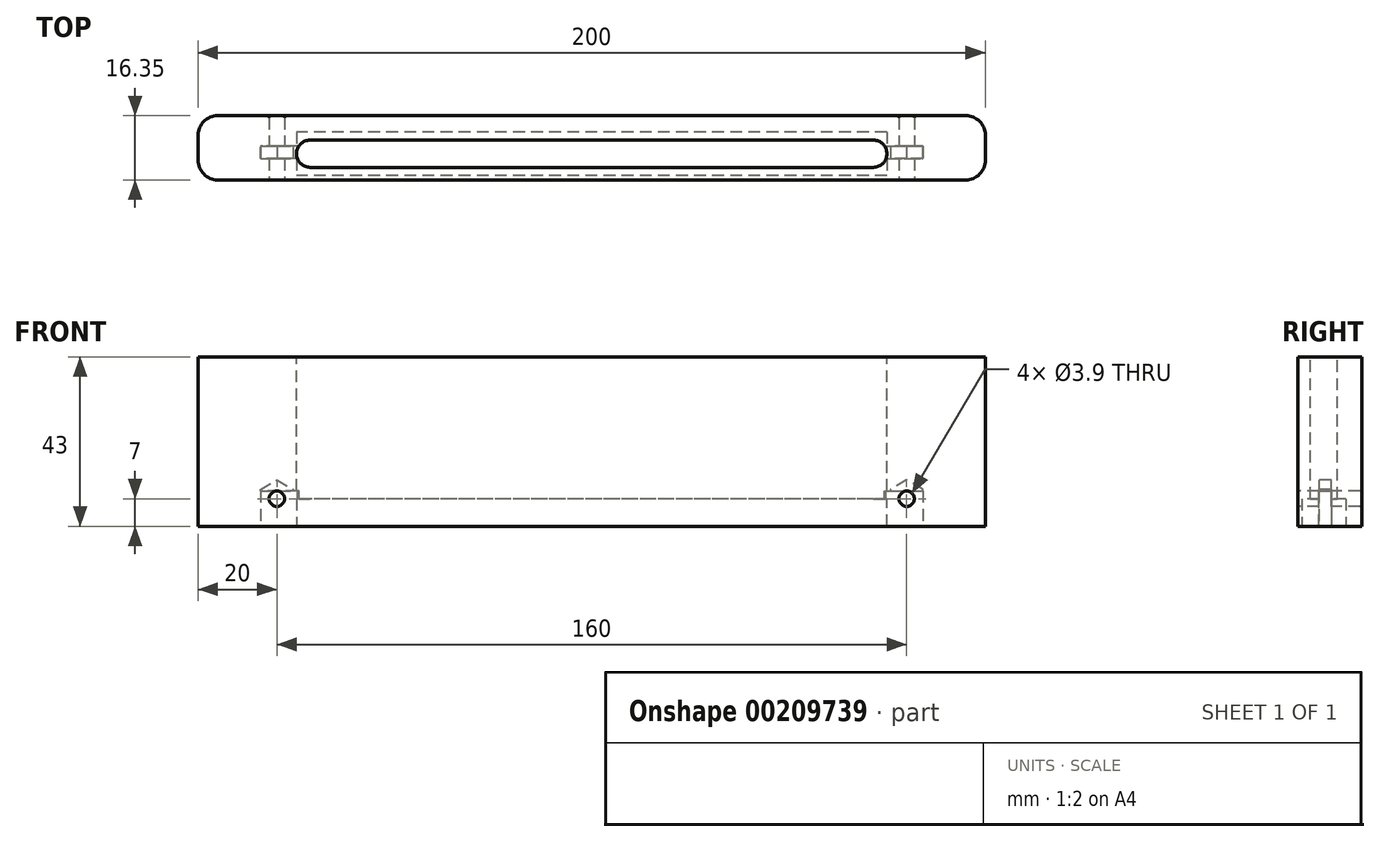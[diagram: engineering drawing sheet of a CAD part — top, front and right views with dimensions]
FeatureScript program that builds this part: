
annotation { "Feature Type Name" : "Feature", "Feature Type Description" : "" }
export const myFeature = defineFeature(function(context is Context, id is Id, definition is map)
    precondition{}
    {
        {
            var Q0;
            Q0=qCreatedBy(makeId("Top.planeOp"),FACE);
            var sketch = newSketch(context, id + "F0", { "sketchPlane" : qUnion([Q0])});
            skLineSegment(sketch, "E0.bottom", {"start": v(-100, 7) * mm, "end": v(100, 7) * mm});
            skLineSegment(sketch, "E0.top", {"start": v(-100, -7) * mm, "end": v(100, -7) * mm});
            skLineSegment(sketch, "E0.left", {"start": v(-100, 7) * mm, "end": v(-100, -7) * mm});
            skLineSegment(sketch, "E0.right", {"start": v(100, 7) * mm, "end": v(100, -7) * mm});
            skPoint(sketch, "E0.middle", {"position": v(0, 0) * mm});
            skLineSegment(sketch, "E1.top", {"start": v(-100, 9.35) * mm, "end": v(100, 9.35) * mm});
            skLineSegment(sketch, "E1.left", {"start": v(-100, 7) * mm, "end": v(-100, 9.35) * mm});
            skLineSegment(sketch, "E1.right", {"start": v(100, 7) * mm, "end": v(100, 9.35) * mm});
            skSolve(sketch);
        }
        {
            var Q0;
            Q0 = qSketchRegion(id + "F0", true);
            extrude(context, id + "F1", {"entities" : qUnion([Q0]), "depth" : 43 * mm});
        }
        {
            var Q0;
            Q0=makeQuery(id+"F1.opExtrude","CAP_FACE",FACE,{"disambiguationData":[OSD([sQuery(id+"F0.wireOp",EDGE,"E0.bottom"),sQuery(id+"F0.wireOp",EDGE,"E0.top"),sQuery(id+"F0.wireOp",EDGE,"E0.left"),sQuery(id+"F0.wireOp",EDGE,"E0.right")])],"isStart":false});
            var sketch = newSketch(context, id + "F2", { "sketchPlane" : qUnion([Q0])});
            skCircle(sketch, "E2", {"center": v(-22, 0) * mm, "radius": 3.45 * mm});
            skSolve(sketch);
        }
        {
            var Q0;
            Q0=makeQuery(id+"F1.opExtrude","CAP_FACE",FACE,{"disambiguationData":[OSD([sQuery(id+"F0.wireOp",EDGE,"E0.bottom"),sQuery(id+"F0.wireOp",EDGE,"E0.top"),sQuery(id+"F0.wireOp",EDGE,"E0.left"),sQuery(id+"F0.wireOp",EDGE,"E0.right")])],"isStart":true});
            var sketch = newSketch(context, id + "F3", { "sketchPlane" : qUnion([Q0])});
            skPoint(sketch, "E3", {"position": v(-22, 0) * mm});
            skPoint(sketch, "E4.MirrorP", {"position": v(22, 0) * mm});
            skLineSegment(sketch, "E5", {"start": v(-25.2, 5.54) * mm, "end": v(-18.8, 5.54) * mm});
            skLineSegment(sketch, "E6", {"start": v(-25.2, 5.54) * mm, "end": v(-28.4, 0) * mm});
            skLineSegment(sketch, "E7", {"start": v(-28.4, 0) * mm, "end": v(-25.2, -5.54) * mm});
            skLineSegment(sketch, "E8", {"start": v(-25.2, -5.54) * mm, "end": v(-18.8, -5.54) * mm});
            skLineSegment(sketch, "E9", {"start": v(-18.8, -5.54) * mm, "end": v(-15.6, 0) * mm});
            skLineSegment(sketch, "E10", {"start": v(-15.6, 0) * mm, "end": v(-18.8, 5.54) * mm});
            skLineSegment(sketch, "E11", {"start": v(-22, 0) * mm, "end": v(-22, 0) * mm, "construction": true});
            skPoint(sketch, "E11.startSnap0", {"position": v(-22, 5.54) * mm});
            skPoint(sketch, "E11.endSnap0", {"position": v(-22, -5.54) * mm});
            skLineSegment(sketch, "E12.MirrorCS", {"start": v(15.6, 0) * mm, "end": v(18.8, 5.54) * mm});
            skLineSegment(sketch, "E13.MirrorCS", {"start": v(25.2, 5.54) * mm, "end": v(18.8, 5.54) * mm});
            skLineSegment(sketch, "E14.MirrorCS", {"start": v(25.2, 5.54) * mm, "end": v(28.4, 0) * mm});
            skLineSegment(sketch, "E15.MirrorCS", {"start": v(28.4, 0) * mm, "end": v(25.2, -5.54) * mm});
            skLineSegment(sketch, "E16.MirrorCS", {"start": v(25.2, -5.54) * mm, "end": v(18.8, -5.54) * mm});
            skLineSegment(sketch, "E17.MirrorCS", {"start": v(18.8, -5.54) * mm, "end": v(15.6, 0) * mm});
            skSolve(sketch);
        }
        {
            var Q0;
            Q0=makeQuery(id+"F1.opExtrude","CAP_FACE",FACE,{"disambiguationData":[OSD([sQuery(id+"F0.wireOp",EDGE,"E0.bottom"),sQuery(id+"F0.wireOp",EDGE,"E0.top"),sQuery(id+"F0.wireOp",EDGE,"E0.left"),sQuery(id+"F0.wireOp",EDGE,"E0.right")])],"isStart":true});
            var sketch = newSketch(context, id + "F4", { "sketchPlane" : qUnion([Q0])});
            skLineSegment(sketch, "E18.bottom", {"start": v(75, -5.2) * mm, "end": v(-75, -5.2) * mm});
            skLineSegment(sketch, "E18.top", {"start": v(75, 5.9) * mm, "end": v(-75, 5.9) * mm});
            skLineSegment(sketch, "E18.left", {"start": v(75, -5.2) * mm, "end": v(75, 5.9) * mm});
            skLineSegment(sketch, "E18.right", {"start": v(-75, -5.2) * mm, "end": v(-75, 5.9) * mm});
            skPoint(sketch, "E18.middle", {"position": v(0, 0.35) * mm});
            skSolve(sketch);
        }
        {
            var Q0;
            Q0 = qSketchRegion(id + "F4", true);
            extrude(context, id + "F5", {"entities" : qUnion([Q0]), "operationType" : NewBodyOperationType.REMOVE, "oppositeDirection" : true, "depth" : 7 * mm});
        }
        {
            var Q0;
            Q0=makeQuery(id+"F1.opExtrude","SWEPT_FACE",FACE,{"disambiguationData":[OSD([sQuery(id+"F0.wireOp",EDGE,"E0.top")])]});
            var sketch = newSketch(context, id + "F6", { "sketchPlane" : qUnion([Q0])});
            skPoint(sketch, "E19", {"position": v(-80, 7) * mm});
            skPoint(sketch, "E20.MirrorP", {"position": v(80, 7) * mm});
            skCircle(sketch, "E21", {"center": v(-80, 7) * mm, "radius": 1.95 * mm});
            skCircle(sketch, "E22", {"center": v(80, 7) * mm, "radius": 1.95 * mm});
            skSolve(sketch);
        }
        {
            var Q0;
            Q0 = qSketchRegion(id + "F6", true);
            extrude(context, id + "F7", {"entities" : qUnion([Q0]), "operationType" : NewBodyOperationType.REMOVE, "endBound" : BoundingType.THROUGH_ALL, "oppositeDirection" : true, "depth" : 25 * mm});
        }
        {
            var Q0;
            Q0=makeQuery(id+"F1.opExtrude","CAP_FACE",FACE,{"disambiguationData":[OSD([sQuery(id+"F0.wireOp",EDGE,"E0.bottom"),sQuery(id+"F0.wireOp",EDGE,"E0.top"),sQuery(id+"F0.wireOp",EDGE,"E0.left"),sQuery(id+"F0.wireOp",EDGE,"E0.right")])],"isStart":false});
            var sketch = newSketch(context, id + "F8", { "sketchPlane" : qUnion([Q0])});
            skLineSegment(sketch, "E23", {"start": v(-71.55, -3.8) * mm, "end": v(71.55, -3.8) * mm});
            skPoint(sketch, "E24", {"position": v(0, -3.8) * mm});
            skLineSegment(sketch, "E25", {"start": v(-71.55, 3.1) * mm, "end": v(71.55, 3.1) * mm});
            skPoint(sketch, "E26", {"position": v(0, 3.1) * mm});
            skArc(sketch, "E27", {"start": v(-71.55, 3.1) * mm, "mid": v(-75, -0.35) * mm, "end": v(-71.55, -3.8) * mm});
            skArc(sketch, "E28", {"start": v(71.55, 3.1) * mm, "mid": v(75, -0.35) * mm, "end": v(71.55, -3.8) * mm});
            skSolve(sketch);
        }
        {
            var Q0;
            Q0 = qSketchRegion(id + "F8", true);
            extrude(context, id + "F9", {"entities" : qUnion([Q0]), "operationType" : NewBodyOperationType.REMOVE, "oppositeDirection" : true, "depth" : 37 * mm});
        }
        {
            var Q0;
            Q0=makeQuery(id+"F1.opExtrude","SWEPT_EDGE",EDGE,{"disambiguationData":[OSD([sQuery(id+"F0.wireOp",EDGE,"E0.top"),sQuery(id+"F0.wireOp",EDGE,"E0.left")])]});
            var Q1;
            Q1=makeQuery(id+"F1.opExtrude","SWEPT_EDGE",EDGE,{"disambiguationData":[OSD([sQuery(id+"F0.wireOp",EDGE,"E1.top"),sQuery(id+"F0.wireOp",EDGE,"E1.left")])]});
            var Q2;
            Q2=makeQuery(id+"F1.opExtrude","SWEPT_EDGE",EDGE,{"disambiguationData":[OSD([sQuery(id+"F0.wireOp",EDGE,"E0.top"),sQuery(id+"F0.wireOp",EDGE,"E0.right")])]});
            var Q3;
            Q3=makeQuery(id+"F1.opExtrude","SWEPT_EDGE",EDGE,{"disambiguationData":[OSD([sQuery(id+"F0.wireOp",EDGE,"E1.top"),sQuery(id+"F0.wireOp",EDGE,"E1.right")])]});
            fillet(context, id + "F10", {"entities" : qUnion([Q0, Q1, Q2, Q3]), "radius" : 5 * mm, "tangentPropagation" : true, "allowEdgeOverflow" : false});
        }
        {
            var Q0;
            Q0=makeQuery(id+"F7.boolean.opBoolean","INTERSECT",EDGE,{"derivedFrom":[makeQuery(id+"F1.opExtrude","SWEPT_FACE",FACE,{"disambiguationData":[OSD([sQuery(id+"F0.wireOp",EDGE,"E1.top")])]}),makeQuery(id+"F7.opExtrude","SWEPT_FACE",FACE,{"disambiguationData":[OSD([sQuery(id+"F6.wireOp",EDGE,"E22")])]})]});
            var Q1;
            Q1=makeQuery(id+"F7.boolean.opBoolean","COPY",EDGE,{"derivedFrom":makeQuery(id+"F7.opExtrude","CAP_EDGE",EDGE,{"disambiguationData":[OSD([sQuery(id+"F6.wireOp",EDGE,"E22")])],"isStart":true})});
            var Q2;
            Q2=makeQuery(id+"F7.boolean.opBoolean","COPY",EDGE,{"derivedFrom":makeQuery(id+"F7.opExtrude","CAP_EDGE",EDGE,{"disambiguationData":[OSD([sQuery(id+"F6.wireOp",EDGE,"E21")])],"isStart":true})});
            var Q3;
            Q3=makeQuery(id+"F7.boolean.opBoolean","INTERSECT",EDGE,{"derivedFrom":[makeQuery(id+"F1.opExtrude","SWEPT_FACE",FACE,{"disambiguationData":[OSD([sQuery(id+"F0.wireOp",EDGE,"E1.top")])]}),makeQuery(id+"F7.opExtrude","SWEPT_FACE",FACE,{"disambiguationData":[OSD([sQuery(id+"F6.wireOp",EDGE,"E21")])]})]});
            fillet(context, id + "F11", {"entities" : qUnion([Q0, Q1, Q2, Q3]), "radius" : .5 * mm, "tangentPropagation" : true, "allowEdgeOverflow" : false});
        }
        {
            var Q0;
            Q0=qCreatedBy(makeId("Front.planeOp"),FACE);
            var sketch = newSketch(context, id + "F12", { "sketchPlane" : qUnion([Q0])});
            skCircle(sketch, "E29.cCircle", {"center": v(-80, 7) * mm, "radius": 4.15 * mm, "construction": true});
            skLineSegment(sketch, "E29.0", {"start": v(-75.85, 9.4) * mm, "end": v(-75.85, 4.6) * mm});
            skLineSegment(sketch, "E29.1", {"start": v(-75.85, 4.6) * mm, "end": v(-80, 2.2) * mm});
            skLineSegment(sketch, "E29.2", {"start": v(-80, 2.2) * mm, "end": v(-84.15, 4.6) * mm});
            skLineSegment(sketch, "E29.3", {"start": v(-84.15, 4.6) * mm, "end": v(-84.15, 9.4) * mm});
            skLineSegment(sketch, "E29.4", {"start": v(-84.15, 9.4) * mm, "end": v(-80, 11.8) * mm});
            skLineSegment(sketch, "E29.5", {"start": v(-80, 11.8) * mm, "end": v(-75.85, 9.4) * mm});
            skPoint(sketch, "E29.0.midPoint", {"position": v(-75.85, 7) * mm});
            skLineSegment(sketch, "E30", {"start": v(0, 43.74) * mm, "end": v(0, -9.53) * mm, "construction": true});
            skLineSegment(sketch, "E31.MirrorCS", {"start": v(84.15, 9.4) * mm, "end": v(80, 11.8) * mm});
            skLineSegment(sketch, "E32.MirrorCS", {"start": v(80, 2.2) * mm, "end": v(84.15, 4.6) * mm});
            skLineSegment(sketch, "E33.MirrorCS", {"start": v(84.15, 4.6) * mm, "end": v(84.15, 9.4) * mm});
            skPoint(sketch, "E34.MirrorP", {"position": v(75.85, 7) * mm});
            skLineSegment(sketch, "E35.MirrorCS", {"start": v(75.85, 9.4) * mm, "end": v(75.85, 4.6) * mm});
            skLineSegment(sketch, "E36.MirrorCS", {"start": v(75.85, 4.6) * mm, "end": v(80, 2.2) * mm});
            skLineSegment(sketch, "E37.MirrorCS", {"start": v(80, 11.8) * mm, "end": v(75.85, 9.4) * mm});
            skCircle(sketch, "E38.MirrorC", {"center": v(80, 7) * mm, "radius": 4.15 * mm, "construction": true});
            skSolve(sketch);
        }
        {
            var Q0;
            Q0 = qSketchRegion(id + "F12", true);
            extrude(context, id + "F13", {"entities" : qUnion([Q0]), "operationType" : NewBodyOperationType.REMOVE, "endBound" : BoundingType.SYMMETRIC, "oppositeDirection" : true, "depth" : 3.1 * mm});
        }
        {
            var Q0;
            Q0=makeQuery(id+"F1.opExtrude","CAP_FACE",FACE,{"disambiguationData":[OSD([sQuery(id+"F0.wireOp",EDGE,"E0.top"),sQuery(id+"F0.wireOp",EDGE,"E0.left"),sQuery(id+"F0.wireOp",EDGE,"E0.right"),sQuery(id+"F0.wireOp",EDGE,"E1.top"),sQuery(id+"F0.wireOp",EDGE,"E1.left"),sQuery(id+"F0.wireOp",EDGE,"E1.right")])],"isStart":true});
            var sketch = newSketch(context, id + "F14", { "sketchPlane" : qUnion([Q0])});
            skLineSegment(sketch, "E39.bottom", {"start": v(-65.85, 1.6) * mm, "end": v(-84.15, 1.6) * mm});
            skLineSegment(sketch, "E39.top", {"start": v(-65.85, -1.6) * mm, "end": v(-84.15, -1.6) * mm});
            skLineSegment(sketch, "E39.left", {"start": v(-65.85, 1.6) * mm, "end": v(-65.85, -1.6) * mm});
            skLineSegment(sketch, "E39.right", {"start": v(-84.15, 1.6) * mm, "end": v(-84.15, -1.6) * mm});
            skPoint(sketch, "E39.middle", {"position": v(-75, 0) * mm});
            skLineSegment(sketch, "E40", {"start": v(0, 35.75) * mm, "end": v(0, -24.7) * mm, "construction": true});
            skLineSegment(sketch, "E41.MirrorCS", {"start": v(65.85, 1.6) * mm, "end": v(84.15, 1.6) * mm});
            skLineSegment(sketch, "E42.MirrorCS", {"start": v(65.85, -1.6) * mm, "end": v(84.15, -1.6) * mm});
            skLineSegment(sketch, "E43.MirrorCS", {"start": v(65.85, 1.6) * mm, "end": v(65.85, -1.6) * mm});
            skLineSegment(sketch, "E44.MirrorCS", {"start": v(84.15, 1.6) * mm, "end": v(84.15, -1.6) * mm});
            skPoint(sketch, "E45.MirrorP", {"position": v(75, 0) * mm});
            skSolve(sketch);
        }
        {
            var Q0;
            Q0 = qSketchRegion(id + "F14", true);
            extrude(context, id + "F15", {"entities" : qUnion([Q0]), "operationType" : NewBodyOperationType.REMOVE, "oppositeDirection" : true, "depth" : 9 * mm});
        }
    });
